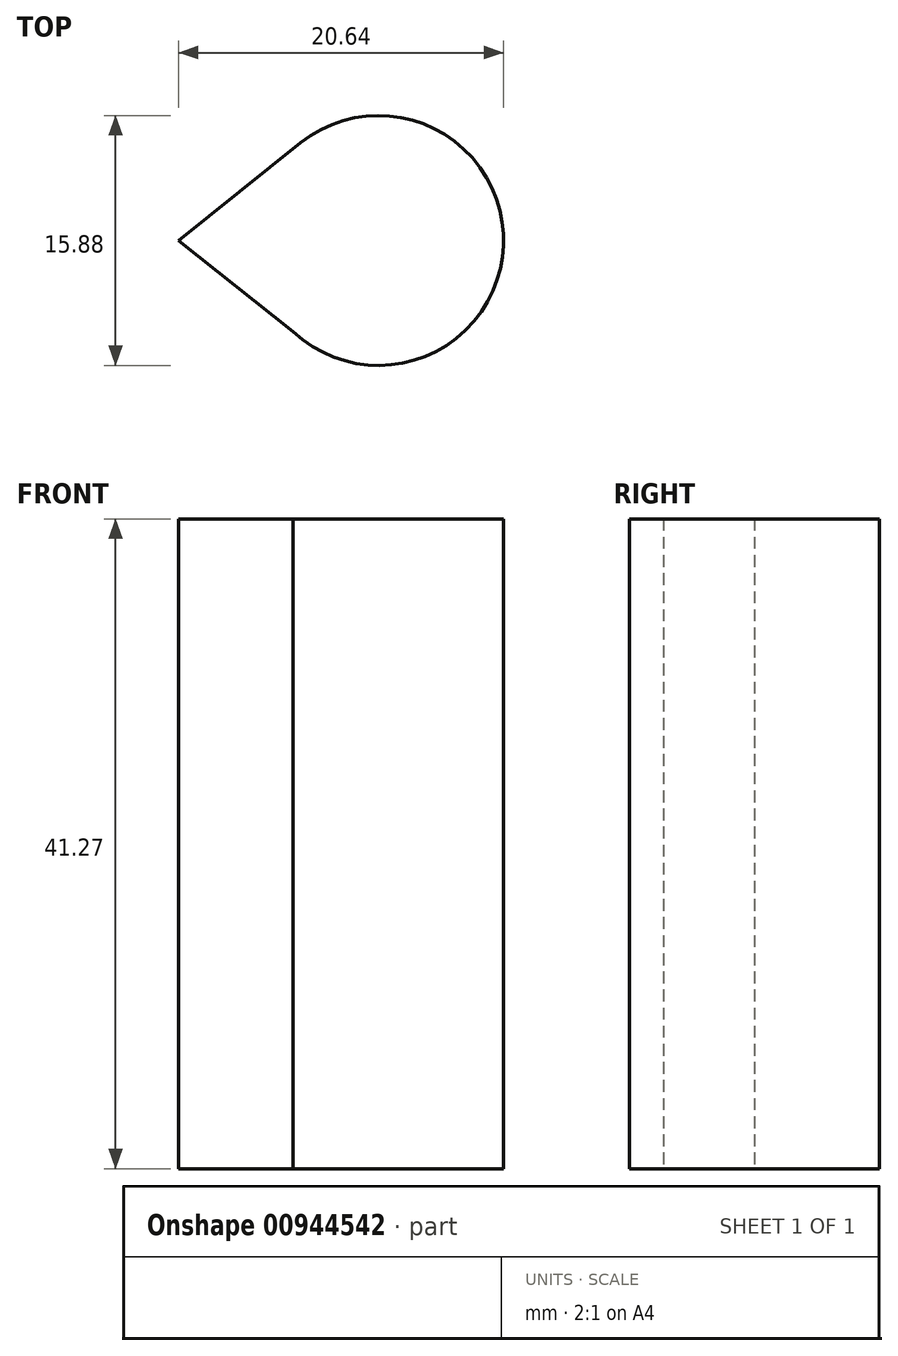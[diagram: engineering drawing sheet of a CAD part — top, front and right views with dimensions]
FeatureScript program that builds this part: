
annotation { "Feature Type Name" : "Feature", "Feature Type Description" : "" }
export const myFeature = defineFeature(function(context is Context, id is Id, definition is map)
    precondition{}
    {
        {
            var Q0;
            Q0=qCreatedBy(makeId("Top.planeOp"),FACE);
            var sketch = newSketch(context, id + "F0", { "sketchPlane" : qUnion([Q0])});
            skCircle(sketch, "E0", {"center": v(0, 0) * mm, "radius": 7.94 * mm});
            skLineSegment(sketch, "E1", {"start": v(-12.7, 0) * mm, "end": v(-4.96, 6.2) * mm});
            skLineSegment(sketch, "E2", {"start": v(-12.7, 0) * mm, "end": v(-5.44, -5.78) * mm});
            skSolve(sketch);
        }
        {
            var Q0;
            {var subQ0=sQuery(id+"F0.wireOp",EDGE,"E1");Q0=makeQuery(id+"F0.imprint","IMPRINT",FACE,{"disambiguationData":[TD([[makeQuery(id+"F0.imprint","IMPRINT",EDGE,{"derivedFrom":subQ0}),-1.0]])]});}
            var Q1;
            {var subQ0=sQuery(id+"F0.wireOp",EDGE,"E0");var subQ1=makeQuery(id+"F0.imprint","INTERSECT",VERTEX,{"derivedFrom":[subQ0,sQuery(id+"F0.wireOp",EDGE,"E1")]});Q1=makeQuery(id+"F0.imprint","IMPRINT",FACE,{"disambiguationData":[TD([[makeQuery(id+"F0.imprint","IMPRINT",EDGE,{"disambiguationData":[TD([[subQ1,-1.0]])],"derivedFrom":subQ0}),1.0]])]});}
            extrude(context, id + "F1", {"entities" : qUnion([Q0, Q1]), "depth" : 41.27 * mm, "offsetDistance" : 25.4 * mm});
        }
    });
